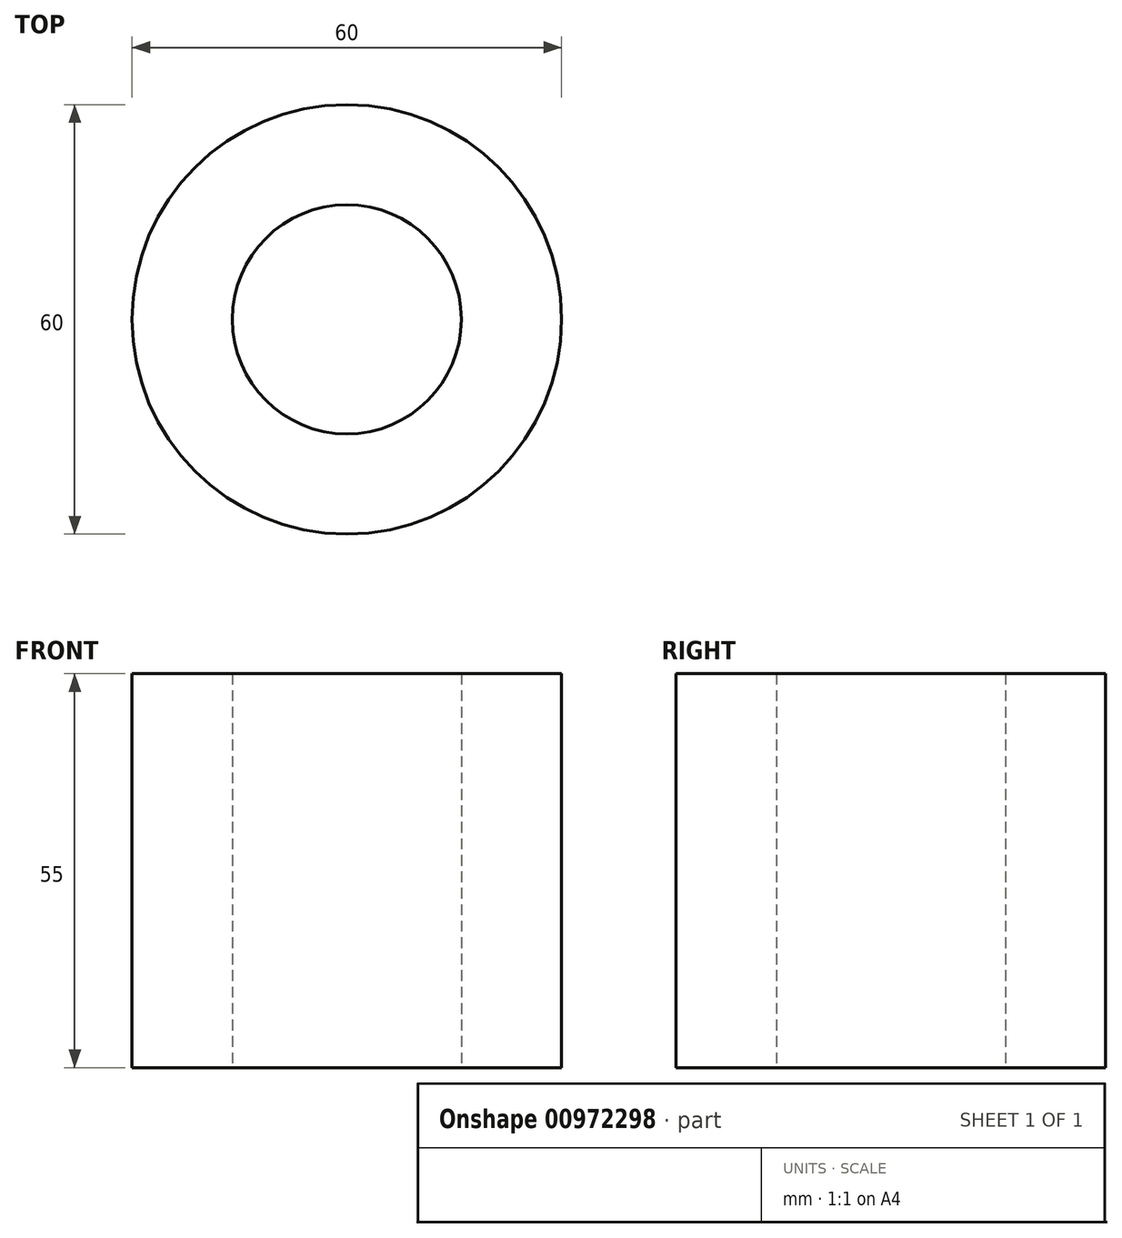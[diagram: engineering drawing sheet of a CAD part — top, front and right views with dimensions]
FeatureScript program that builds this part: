
annotation { "Feature Type Name" : "Feature", "Feature Type Description" : "" }
export const myFeature = defineFeature(function(context is Context, id is Id, definition is map)
    precondition{}
    {
        {
            var Q0;
            Q0=qCreatedBy(makeId("Top.planeOp"),FACE);
            var sketch = newSketch(context, id + "F0", { "sketchPlane" : qUnion([Q0])});
            skCircle(sketch, "E0", {"center": v(0, 0) * mm, "radius": 30 * mm});
            skCircle(sketch, "E1", {"center": v(0, 0) * mm, "radius": 16 * mm});
            skSolve(sketch);
        }
        {
            var Q0;
            Q0=makeQuery(id+"F0.imprint","IMPRINT",FACE,{"disambiguationData":[TD([[makeQuery(id+"F0.imprint","IMPRINT",EDGE,{"derivedFrom":sQuery(id+"F0.wireOp",EDGE,"E0")}),1.0]])]});
            extrude(context, id + "F1", {"entities" : qUnion([Q0]), "depth" : 55 * mm, "offsetDistance" : 25 * mm});
        }
    });
